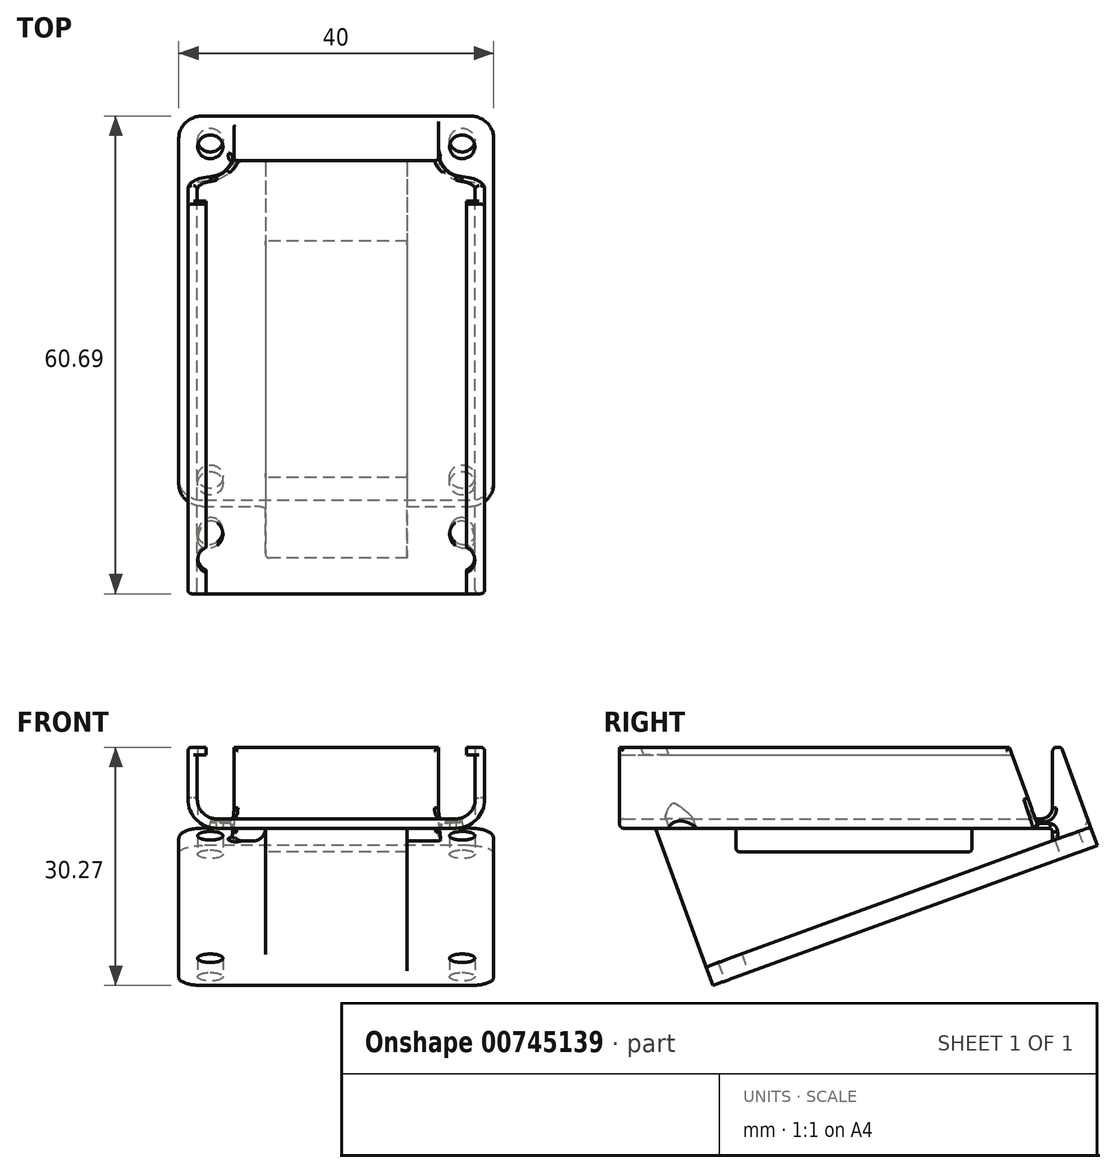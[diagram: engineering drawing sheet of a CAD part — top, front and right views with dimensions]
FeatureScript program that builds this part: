
annotation { "Feature Type Name" : "Feature", "Feature Type Description" : "" }
export const myFeature = defineFeature(function(context is Context, id is Id, definition is map)
    precondition{}
    {
        {
            var Q0;
            Q0=qCreatedBy(makeId("Front.planeOp"),FACE);
            var sketch = newSketch(context, id + "F0", { "sketchPlane" : qUnion([Q0])});
            skLineSegment(sketch, "E0", {"start": v(-15.15, 0) * mm, "end": v(15.15, 0) * mm});
            skLineSegment(sketch, "E1", {"start": v(-18.85, 3.7) * mm, "end": v(-18.85, 10.3) * mm});
            skLineSegment(sketch, "E2", {"start": v(-18.85, 10.3) * mm, "end": v(-16.55, 10.3) * mm});
            skLineSegment(sketch, "E3", {"start": v(-16.55, 10.3) * mm, "end": v(-16.55, 9.3) * mm});
            skLineSegment(sketch, "E4", {"start": v(-16.55, 9.3) * mm, "end": v(-17.65, 9.3) * mm});
            skLineSegment(sketch, "E5", {"start": v(-17.65, 9.3) * mm, "end": v(-17.65, 3.7) * mm});
            skLineSegment(sketch, "E6", {"start": v(17.65, 3.7) * mm, "end": v(17.65, 9.3) * mm});
            skLineSegment(sketch, "E7", {"start": v(17.65, 9.3) * mm, "end": v(16.55, 9.3) * mm});
            skLineSegment(sketch, "E8", {"start": v(16.55, 9.3) * mm, "end": v(16.55, 10.3) * mm});
            skLineSegment(sketch, "E9", {"start": v(16.55, 10.3) * mm, "end": v(18.85, 10.3) * mm});
            skLineSegment(sketch, "E10", {"start": v(18.85, 10.3) * mm, "end": v(18.85, 3.7) * mm});
            skLineSegment(sketch, "E11", {"start": v(-15.15, 1.2) * mm, "end": v(15.15, 1.2) * mm});
            skArc(sketch, "E12", {"start": v(17.65, 3.7) * mm, "mid": v(16.92, 1.93) * mm, "end": v(15.15, 1.2) * mm});
            skArc(sketch, "E13", {"start": v(-15.15, 1.2) * mm, "mid": v(-16.92, 1.93) * mm, "end": v(-17.65, 3.7) * mm});
            skArc(sketch, "E14", {"start": v(-18.85, 3.7) * mm, "mid": v(-17.77, 1.08) * mm, "end": v(-15.15, 0) * mm});
            skArc(sketch, "E15", {"start": v(15.15, 0) * mm, "mid": v(17.77, 1.08) * mm, "end": v(18.85, 3.7) * mm});
            skSolve(sketch);
        }
        {
            var Q0;
            Q0=qSketchRegion(id+"F0",true);
            extrude(context, id + "F1", {"entities" : qUnion([Q0]), "depth" : 55 * mm, "offsetDistance" : 25 * mm});
        }
        {
            var Q0;
            Q0=qCreatedBy(makeId("Right.planeOp"),FACE);
            var sketch = newSketch(context, id + "F2", { "sketchPlane" : qUnion([Q0])});
            skLineSegment(sketch, "E16", {"start": v(4.83, 0.16) * mm, "end": v(-44.03, -17.62) * mm});
            skPoint(sketch, "E17.0", {"position": v(-50.45, 0) * mm});
            skLineSegment(sketch, "E18", {"start": v(-50.45, 0) * mm, "end": v(-44.03, -17.62) * mm});
            skPoint(sketch, "E19.0", {"position": v(0, 10.3) * mm});
            skLineSegment(sketch, "E20", {"start": v(1.14, 10.3) * mm, "end": v(4.83, 0.16) * mm});
            skLineSegment(sketch, "E21", {"start": v(1.14, 10.3) * mm, "end": v(0, 10.3) * mm});
            skLineSegment(sketch, "E22", {"start": v(0, 0) * mm, "end": v(-50.45, 0) * mm});
            skLineSegment(sketch, "E23", {"start": v(4.83, 0.16) * mm, "end": v(5.69, -2.19) * mm});
            skLineSegment(sketch, "E24", {"start": v(5.69, -2.19) * mm, "end": v(-43.18, -19.97) * mm});
            skLineSegment(sketch, "E25", {"start": v(-43.18, -19.97) * mm, "end": v(-44.03, -17.62) * mm});
            skPoint(sketch, "E26", {"position": v(-25.22, 0) * mm});
            skLineSegment(sketch, "E27.bottom", {"start": v(-10.22, 0) * mm, "end": v(-40.22, 0) * mm});
            skLineSegment(sketch, "E27.top", {"start": v(-10.22, -3) * mm, "end": v(-40.22, -3) * mm});
            skLineSegment(sketch, "E27.left", {"start": v(-10.22, 0) * mm, "end": v(-10.22, -3) * mm});
            skLineSegment(sketch, "E27.right", {"start": v(-40.22, 0) * mm, "end": v(-40.22, -3) * mm});
            skLineSegment(sketch, "E28", {"start": v(0, 0) * mm, "end": v(0, 10.3) * mm});
            skLineSegment(sketch, "E29", {"start": v(0, 0) * mm, "end": v(0, -1.6) * mm});
            skSolve(sketch);
        }
        {
            var Q0;
            {var subQ0=sQuery(id+"F2.wireOp",EDGE,"E20");Q0=makeQuery(id+"F2.imprint","IMPRINT",FACE,{"disambiguationData":[TD([[makeQuery(id+"F2.imprint","IMPRINT",EDGE,{"derivedFrom":subQ0}),-1.0]])]});}
            var Q1;
            Q1=makeQuery(id+"F1.opExtrude","SWEPT_FACE",FACE,{"disambiguationData":[OSD([sQuery(id+"F0.wireOp",EDGE,"E1")])]});
            extrude(context, id + "F3", {"entities" : qUnion([Q0]), "operationType" : NewBodyOperationType.ADD, "endBound" : BoundingType.UP_TO_SURFACE, "oppositeDirection" : true, "depth" : 25 * mm, "endBoundEntityFace" : qUnion([Q1]), "offsetDistance" : 25 * mm});
        }
        {
            var Q0;
            {var subQ0=sQuery(id+"F2.wireOp",EDGE,"E20");Q0=makeQuery(id+"F2.imprint","IMPRINT",FACE,{"disambiguationData":[TD([[makeQuery(id+"F2.imprint","IMPRINT",EDGE,{"derivedFrom":subQ0}),-1.0]])]});}
            var Q1;
            Q1=makeQuery(id+"F1.opExtrude","SWEPT_FACE",FACE,{"disambiguationData":[OSD([sQuery(id+"F0.wireOp",EDGE,"E10")])]});
            extrude(context, id + "F4", {"entities" : qUnion([Q0]), "operationType" : NewBodyOperationType.ADD, "endBound" : BoundingType.UP_TO_SURFACE, "depth" : 25 * mm, "endBoundEntityFace" : qUnion([Q1]), "offsetDistance" : 25 * mm});
        }
        {
            var Q0;
            {var subQ0=sQuery(id+"F2.wireOp",EDGE,"E23");Q0=makeQuery(id+"F2.imprint","IMPRINT",FACE,{"disambiguationData":[TD([[makeQuery(id+"F2.imprint","IMPRINT",EDGE,{"derivedFrom":subQ0}),-1.0]])]});}
            extrude(context, id + "F5", {"entities" : qUnion([Q0]), "operationType" : NewBodyOperationType.ADD, "endBound" : BoundingType.SYMMETRIC, "depth" : 40 * mm, "offsetDistance" : 25 * mm});
        }
        {
            var Q0;
            {var subQ4=sQuery(id+"F2.wireOp",EDGE,"E18");Q0=makeQuery(id+"F2.imprint","IMPRINT",FACE,{"disambiguationData":[TD([[makeQuery(id+"F2.imprint","IMPRINT",EDGE,{"derivedFrom":subQ4}),1.0]])]});}
            extrude(context, id + "F6", {"entities" : qUnion([Q0]), "operationType" : NewBodyOperationType.ADD, "endBound" : BoundingType.SYMMETRIC, "depth" : 18 * mm, "offsetDistance" : 25 * mm});
        }
        {
            var Q0;
            Q0=makeQuery(id+"F5.opExtrude","SWEPT_FACE",FACE,{"disambiguationData":[OSD([sQuery(id+"F2.wireOp",EDGE,"E24")])]});
            var sketch = newSketch(context, id + "F7", { "sketchPlane" : qUnion([Q0])});
            skCircle(sketch, "E30", {"center": v(-16, -1.35) * mm, "radius": 1.6 * mm});
            skCircle(sketch, "E31", {"center": v(-16, 44.15) * mm, "radius": 1.6 * mm});
            skCircle(sketch, "E32", {"center": v(16, 44.15) * mm, "radius": 1.6 * mm});
            skCircle(sketch, "E33", {"center": v(16, -1.35) * mm, "radius": 1.6 * mm});
            skLineSegment(sketch, "E34", {"start": v(-16, 44.15) * mm, "end": v(-16, 47.4) * mm, "construction": true});
            skLineSegment(sketch, "E35", {"start": v(-16, -1.35) * mm, "end": v(-16, -4.6) * mm, "construction": true});
            skSolve(sketch);
        }
        {
            var Q0;
            Q0 = qSketchRegion(id + "F7", true);
            extrude(context, id + "F8", {"entities" : qUnion([Q0]), "operationType" : NewBodyOperationType.REMOVE, "endBound" : BoundingType.THROUGH_ALL, "oppositeDirection" : true, "depth" : 25 * mm, "offsetDistance" : 25 * mm});
        }
        {
            var Q0;
            {var subQ2=sQuery(id+"F2.wireOp",EDGE,"E16");var subQ4=sQuery(id+"F0.wireOp",EDGE,"E10");Q0=makeQuery(id+"F6.boolean.opBoolean","SPLIT",FACE,{"disambiguationData":[TD([makeQuery(id+"F1.opExtrude","SWEPT_FACE",FACE,{"disambiguationData":[OSD([subQ4])]})])],"derivedFrom":makeQuery(id+"F5.opExtrude","SWEPT_FACE",FACE,{"disambiguationData":[OSD([subQ2])]})});}
            cPlane(context, id + "F9", {"entities" : qUnion([Q0]), "cplaneType" : CPlaneType.OFFSET, "offset" : 0 * mm, "width" : 150 * mm, "height" : 150 * mm});
        }
        {
            var Q0;
            Q0=qCreatedBy(id+"F9.planeOp",FACE);
            var sketch = newSketch(context, id + "F10", { "sketchPlane" : qUnion([Q0])});
            skCircle(sketch, "E36.0", {"center": v(16, 1.35) * mm, "radius": 1.6 * mm});
            skCircle(sketch, "E37.0", {"center": v(-16, 1.35) * mm, "radius": 1.6 * mm});
            skLineSegment(sketch, "E38.0", {"start": v(20, 4.6) * mm, "end": v(-20, 4.6) * mm});
            skLineSegment(sketch, "E39.0", {"start": v(20, 4.6) * mm, "end": v(20, -47.4) * mm});
            skLineSegment(sketch, "E40.0", {"start": v(-20, 4.6) * mm, "end": v(-20, -47.4) * mm});
            skArc(sketch, "E41", {"start": v(-16, -1.65) * mm, "mid": v(-13.88, -0.78) * mm, "end": v(-13, 1.35) * mm});
            skArc(sketch, "E42", {"start": v(13, 1.35) * mm, "mid": v(13.88, -0.78) * mm, "end": v(16, -1.65) * mm});
            skLineSegment(sketch, "E43", {"start": v(16, -1.65) * mm, "end": v(20, -1.65) * mm});
            skLineSegment(sketch, "E44", {"start": v(13, 1.35) * mm, "end": v(13, 4.6) * mm});
            skLineSegment(sketch, "E45", {"start": v(-16, -1.65) * mm, "end": v(-20, -1.65) * mm});
            skLineSegment(sketch, "E46", {"start": v(-13, 1.35) * mm, "end": v(-13, 4.6) * mm});
            skSolve(sketch);
        }
        {
            var Q0;
            Q0 = qSketchRegion(id + "F10", true);
            extrude(context, id + "F11", {"entities" : qUnion([Q0]), "operationType" : NewBodyOperationType.REMOVE, "endBound" : BoundingType.THROUGH_ALL, "depth" : 25 * mm, "offsetDistance" : 25 * mm});
        }
        {
            var Q0;
            Q0=makeQuery(id+"F5.opExtrude","CAP_EDGE",EDGE,{"disambiguationData":[OSD([sQuery(id+"F2.wireOp",EDGE,"E25")])],"isStart":true});
            var Q1;
            Q1=makeQuery(id+"F5.opExtrude","CAP_EDGE",EDGE,{"disambiguationData":[OSD([sQuery(id+"F2.wireOp",EDGE,"E23")])],"isStart":true});
            var Q2;
            Q2=makeQuery(id+"F5.opExtrude","CAP_EDGE",EDGE,{"disambiguationData":[OSD([sQuery(id+"F2.wireOp",EDGE,"E23")])],"isStart":false});
            var Q3;
            Q3=makeQuery(id+"F5.opExtrude","CAP_EDGE",EDGE,{"disambiguationData":[OSD([sQuery(id+"F2.wireOp",EDGE,"E25")])],"isStart":false});
            fillet(context, id + "F12", {"entities" : qUnion([Q0, Q1, Q2, Q3]), "radius" : 3 * mm, "tangentPropagation" : true, "allowEdgeOverflow" : false});
        }
        {
            var Q0;
            Q0=makeQuery(id+"F6.opExtrude","CAP_EDGE",EDGE,{"disambiguationData":[OSD([sQuery(id+"F2.wireOp",EDGE,"E16")])],"isStart":false});
            var Q1;
            {var subQ0=sQuery(id+"F2.wireOp",EDGE,"E22");Q1=makeQuery(id+"F6.opExtrude","CAP_EDGE",EDGE,{"disambiguationData":[OSD([subQ0]),TDD([makeQuery(id+"F2.imprint","IMPRINT",EDGE,{"disambiguationData":[TD([[makeQuery(id+"F2.imprint","INTERSECT",VERTEX,{"derivedFrom":[subQ0,sQuery(id+"F2.wireOp",EDGE,"E28"),sQuery(id+"F2.wireOp",EDGE,"E29")]}),-1.0]])],"derivedFrom":subQ0})])],"isStart":false});}
            var Q2;
            {var subQ0=sQuery(id+"F2.wireOp",EDGE,"E22");Q2=makeQuery(id+"F6.opExtrude","CAP_EDGE",EDGE,{"disambiguationData":[OSD([subQ0]),TDD([makeQuery(id+"F2.imprint","IMPRINT",EDGE,{"disambiguationData":[TD([[makeQuery(id+"F2.imprint","INTERSECT",VERTEX,{"derivedFrom":[sQuery(id+"F2.wireOp",EDGE,"E18"),subQ0]}),1.0]])],"derivedFrom":subQ0})])],"isStart":false});}
            var Q3;
            {var subQ0=sQuery(id+"F2.wireOp",EDGE,"E22");Q3=makeQuery(id+"F6.opExtrude","CAP_EDGE",EDGE,{"disambiguationData":[OSD([subQ0]),TDD([makeQuery(id+"F2.imprint","IMPRINT",EDGE,{"disambiguationData":[TD([[makeQuery(id+"F2.imprint","INTERSECT",VERTEX,{"derivedFrom":[sQuery(id+"F2.wireOp",EDGE,"E18"),subQ0]}),1.0]])],"derivedFrom":subQ0})])],"isStart":true});}
            var Q4;
            Q4=makeQuery(id+"F6.opExtrude","CAP_EDGE",EDGE,{"disambiguationData":[OSD([sQuery(id+"F2.wireOp",EDGE,"E16")])],"isStart":true});
            var Q5;
            {var subQ0=sQuery(id+"F2.wireOp",EDGE,"E22");Q5=makeQuery(id+"F6.opExtrude","CAP_EDGE",EDGE,{"disambiguationData":[OSD([subQ0]),TDD([makeQuery(id+"F2.imprint","IMPRINT",EDGE,{"disambiguationData":[TD([[makeQuery(id+"F2.imprint","INTERSECT",VERTEX,{"derivedFrom":[subQ0,sQuery(id+"F2.wireOp",EDGE,"E28"),sQuery(id+"F2.wireOp",EDGE,"E29")]}),-1.0]])],"derivedFrom":subQ0})])],"isStart":true});}
            var Q6;
            {var subQ0=sQuery(id+"F0.wireOp",EDGE,"E11");var subQ2=makeQuery(id+"F1.opExtrude","CAP_EDGE",EDGE,{"disambiguationData":[OSD([subQ0])],"isStart":true});Q6=makeQuery(id+"F4.boolean.opBoolean","MERGE",EDGE,{"derivedFrom":[makeQuery(id+"F3.boolean.opBoolean","SPLIT",EDGE,{"disambiguationData":[topologyDisambiguationEdgeConnected([makeQuery(id+"F1.opExtrude","CAP_FACE",FACE,{"disambiguationData":[OSD([sQuery(id+"F0.wireOp",EDGE,"E0"),sQuery(id+"F0.wireOp",EDGE,"E1"),sQuery(id+"F0.wireOp",EDGE,"E2"),sQuery(id+"F0.wireOp",EDGE,"E3"),sQuery(id+"F0.wireOp",EDGE,"E4"),sQuery(id+"F0.wireOp",EDGE,"E5"),sQuery(id+"F0.wireOp",EDGE,"E6"),sQuery(id+"F0.wireOp",EDGE,"E7"),sQuery(id+"F0.wireOp",EDGE,"E8"),sQuery(id+"F0.wireOp",EDGE,"E9"),sQuery(id+"F0.wireOp",EDGE,"E10"),subQ0,sQuery(id+"F0.wireOp",EDGE,"E12"),sQuery(id+"F0.wireOp",EDGE,"E13"),sQuery(id+"F0.wireOp",EDGE,"E14"),sQuery(id+"F0.wireOp",EDGE,"E15")])],"isStart":true})])],"derivedFrom":subQ2}),makeQuery(id+"F3.boolean.opBoolean","SPLIT",EDGE,{"disambiguationData":[topologyDisambiguationEdgeConnected([makeQuery(id+"F3.opExtrude","SWEPT_FACE",FACE,{"disambiguationData":[OSD([sQuery(id+"F2.wireOp",EDGE,"E28"),sQuery(id+"F2.wireOp",EDGE,"E29")])]})])],"derivedFrom":subQ2})]});}
            fillet(context, id + "F13", {"entities" : qUnion([Q0, Q1, Q2, Q3, Q4, Q5, Q6]), "radius" : 1.5 * mm, "tangentPropagation" : true, "allowEdgeOverflow" : false});
        }
        {
            var Q0;
            Q0=makeQuery(id+"F5.opExtrude","CAP_EDGE",EDGE,{"disambiguationData":[OSD([sQuery(id+"F2.wireOp",EDGE,"E16")])],"isStart":true});
            var Q1;
            Q1=makeQuery(id+"F5.opExtrude","CAP_EDGE",EDGE,{"disambiguationData":[OSD([sQuery(id+"F2.wireOp",EDGE,"E16")])],"isStart":false});
            var Q2;
            Q2=makeQuery(id+"F6.opExtrude","SWEPT_EDGE",EDGE,{"disambiguationData":[OSD([sQuery(id+"F2.wireOp",EDGE,"E18"),sQuery(id+"F2.wireOp",EDGE,"E22")])]});
            var Q3;
            Q3=makeQuery(id+"F6.opExtrude","SWEPT_EDGE",EDGE,{"disambiguationData":[OSD([sQuery(id+"F2.wireOp",EDGE,"E22"),sQuery(id+"F2.wireOp",EDGE,"E27.bottom"),sQuery(id+"F2.wireOp",EDGE,"E27.right")])]});
            var Q4;
            Q4=makeQuery(id+"F6.opExtrude","SWEPT_EDGE",EDGE,{"disambiguationData":[OSD([sQuery(id+"F2.wireOp",EDGE,"E27.top"),sQuery(id+"F2.wireOp",EDGE,"E27.right")])]});
            var Q5;
            Q5=makeQuery(id+"F6.opExtrude","SWEPT_EDGE",EDGE,{"disambiguationData":[OSD([sQuery(id+"F2.wireOp",EDGE,"E27.top"),sQuery(id+"F2.wireOp",EDGE,"E27.left")])]});
            var Q6;
            Q6=makeQuery(id+"F6.opExtrude","SWEPT_EDGE",EDGE,{"disambiguationData":[OSD([sQuery(id+"F2.wireOp",EDGE,"E22"),sQuery(id+"F2.wireOp",EDGE,"E27.bottom"),sQuery(id+"F2.wireOp",EDGE,"E27.left")])]});
            var Q7;
            Q7=makeQuery(id+"F11.boolean.opBoolean","COPY",EDGE,{"derivedFrom":makeQuery(id+"F11.opExtrude","SWEPT_EDGE",EDGE,{"disambiguationData":[OSD([sQuery(id+"F10.wireOp",EDGE,"E38.0"),sQuery(id+"F10.wireOp",EDGE,"E46")])]})});
            var Q8;
            {var subQ0=sQuery(id+"F2.wireOp",EDGE,"E21");var subQ1=sQuery(id+"F2.wireOp",EDGE,"E20");Q8=makeQuery(id+"F4.boolean.opBoolean","MERGE",EDGE,{"derivedFrom":[makeQuery(id+"F3.opExtrude","SWEPT_EDGE",EDGE,{"disambiguationData":[OSD([subQ1,subQ0])]}),makeQuery(id+"F4.opExtrude","SWEPT_EDGE",EDGE,{"disambiguationData":[OSD([subQ1,subQ0])]})]});}
            var Q9;
            Q9=makeQuery(id+"F11.boolean.opBoolean","COPY",EDGE,{"derivedFrom":makeQuery(id+"F11.opExtrude","SWEPT_EDGE",EDGE,{"disambiguationData":[OSD([sQuery(id+"F10.wireOp",EDGE,"E38.0"),sQuery(id+"F10.wireOp",EDGE,"E44")])]})});
            var Q10;
            {var subQ0=sQuery(id+"F2.wireOp",EDGE,"E28");var subQ1=sQuery(id+"F2.wireOp",EDGE,"E21");Q10=makeQuery(id+"F4.boolean.opBoolean","MERGE",EDGE,{"derivedFrom":[makeQuery(id+"F3.opExtrude","SWEPT_EDGE",EDGE,{"disambiguationData":[OSD([subQ1,subQ0])]}),makeQuery(id+"F4.opExtrude","SWEPT_EDGE",EDGE,{"disambiguationData":[OSD([subQ1,subQ0])]})]});}
            var Q11;
            {var subQ0=sQuery(id+"F2.wireOp",EDGE,"E29");var subQ1=sQuery(id+"F2.wireOp",EDGE,"E28");var subQ4=sQuery(id+"F0.wireOp",EDGE,"E2");Q11=makeQuery(id+"F11.boolean.opBoolean","INTERSECT",EDGE,{"derivedFrom":[makeQuery(id+"F4.boolean.opBoolean","MERGE",FACE,{"derivedFrom":[makeQuery(id+"F3.boolean.opBoolean","SPLIT",FACE,{"disambiguationData":[TD([makeQuery(id+"F1.opExtrude","SWEPT_FACE",FACE,{"disambiguationData":[OSD([subQ4])]})])],"derivedFrom":makeQuery(id+"F3.opExtrude","SWEPT_FACE",FACE,{"disambiguationData":[OSD([subQ1,subQ0])]})}),makeQuery(id+"F4.opExtrude","SWEPT_FACE",FACE,{"disambiguationData":[OSD([subQ1,subQ0])]})]}),makeQuery(id+"F11.opExtrude","SWEPT_FACE",FACE,{"disambiguationData":[OSD([sQuery(id+"F10.wireOp",EDGE,"E44")])]})]});}
            var Q12;
            {var subQ0=sQuery(id+"F2.wireOp",EDGE,"E29");var subQ1=sQuery(id+"F2.wireOp",EDGE,"E28");var subQ4=sQuery(id+"F0.wireOp",EDGE,"E2");Q12=makeQuery(id+"F11.boolean.opBoolean","INTERSECT",EDGE,{"derivedFrom":[makeQuery(id+"F4.boolean.opBoolean","MERGE",FACE,{"derivedFrom":[makeQuery(id+"F3.boolean.opBoolean","SPLIT",FACE,{"disambiguationData":[TD([makeQuery(id+"F1.opExtrude","SWEPT_FACE",FACE,{"disambiguationData":[OSD([subQ4])]})])],"derivedFrom":makeQuery(id+"F3.opExtrude","SWEPT_FACE",FACE,{"disambiguationData":[OSD([subQ1,subQ0])]})}),makeQuery(id+"F4.opExtrude","SWEPT_FACE",FACE,{"disambiguationData":[OSD([subQ1,subQ0])]})]}),makeQuery(id+"F11.opExtrude","SWEPT_FACE",FACE,{"disambiguationData":[OSD([sQuery(id+"F10.wireOp",EDGE,"E46")])]})]});}
            var Q13;
            {var subQ0=sQuery(id+"F0.wireOp",EDGE,"E1");Q13=makeQuery(id+"F3.boolean.opBoolean","MERGE",EDGE,{"derivedFrom":[makeQuery(id+"F1.opExtrude","SWEPT_EDGE",EDGE,{"disambiguationData":[OSD([subQ0,sQuery(id+"F0.wireOp",EDGE,"E2")])]}),makeQuery(id+"F3.opExtrude","TWEAK_EDGE",EDGE,{"derivedFrom":[makeQuery(id+"F1.opExtrude","SWEPT_FACE",FACE,{"disambiguationData":[OSD([subQ0])]}),makeQuery(id+"F2.imprint","IMPRINT",EDGE,{"derivedFrom":sQuery(id+"F2.wireOp",EDGE,"E21")})]})]});}
            var Q14;
            {var subQ0=sQuery(id+"F0.wireOp",EDGE,"E10");Q14=makeQuery(id+"F4.boolean.opBoolean","MERGE",EDGE,{"derivedFrom":[makeQuery(id+"F1.opExtrude","SWEPT_EDGE",EDGE,{"disambiguationData":[OSD([sQuery(id+"F0.wireOp",EDGE,"E9"),subQ0])]}),makeQuery(id+"F4.opExtrude","TWEAK_EDGE",EDGE,{"derivedFrom":[makeQuery(id+"F1.opExtrude","SWEPT_FACE",FACE,{"disambiguationData":[OSD([subQ0])]}),makeQuery(id+"F2.imprint","IMPRINT",EDGE,{"derivedFrom":sQuery(id+"F2.wireOp",EDGE,"E21")})]})]});}
            var Q15;
            {var subQ0=sQuery(id+"F0.wireOp",EDGE,"E10");Q15=makeQuery(id+"F11.boolean.opBoolean","INTERSECT",EDGE,{"derivedFrom":[makeQuery(id+"F4.boolean.opBoolean","MERGE",FACE,{"derivedFrom":[makeQuery(id+"F1.opExtrude","SWEPT_FACE",FACE,{"disambiguationData":[OSD([subQ0])]}),makeQuery(id+"F4.opExtrude","CAP_FACE",FACE,{"disambiguationData":[OSD([subQ0])],"isStart":false})]}),makeQuery(id+"F11.opExtrude","SWEPT_FACE",FACE,{"disambiguationData":[OSD([sQuery(id+"F10.wireOp",EDGE,"E43")])]})]});}
            var Q16;
            {var subQ0=sQuery(id+"F0.wireOp",EDGE,"E1");Q16=makeQuery(id+"F11.boolean.opBoolean","INTERSECT",EDGE,{"derivedFrom":[makeQuery(id+"F3.boolean.opBoolean","MERGE",FACE,{"derivedFrom":[makeQuery(id+"F1.opExtrude","SWEPT_FACE",FACE,{"disambiguationData":[OSD([subQ0])]}),makeQuery(id+"F3.opExtrude","CAP_FACE",FACE,{"disambiguationData":[OSD([subQ0])],"isStart":false})]}),makeQuery(id+"F11.opExtrude","SWEPT_FACE",FACE,{"disambiguationData":[OSD([sQuery(id+"F10.wireOp",EDGE,"E45")])]})]});}
            var Q17;
            {var subQ0=sQuery(id+"F0.wireOp",EDGE,"E0");var subQ1=makeQuery(id+"F1.opExtrude","SWEPT_FACE",FACE,{"disambiguationData":[OSD([subQ0])]});var subQ2=sQuery(id+"F2.wireOp",EDGE,"E29");var subQ8=sQuery(id+"F0.wireOp",EDGE,"E1");var subQ10=makeQuery(id+"F1.opExtrude","SWEPT_FACE",FACE,{"disambiguationData":[OSD([subQ8])]});var subQ11=sQuery(id+"F2.wireOp",EDGE,"E28");Q17=makeQuery(id+"F11.boolean.opBoolean","INTERSECT",EDGE,{"derivedFrom":[makeQuery(id+"F8.boolean.opBoolean","SPLIT",FACE,{"disambiguationData":[TD([subQ1])],"derivedFrom":makeQuery(id+"F6.boolean.opBoolean","SPLIT",FACE,{"disambiguationData":[TD([subQ10])],"derivedFrom":makeQuery(id+"F4.boolean.opBoolean","MERGE",FACE,{"derivedFrom":[makeQuery(id+"F3.boolean.opBoolean","SPLIT",FACE,{"disambiguationData":[TD([subQ1])],"derivedFrom":makeQuery(id+"F3.opExtrude","SWEPT_FACE",FACE,{"disambiguationData":[OSD([subQ11,subQ2])]})}),makeQuery(id+"F4.opExtrude","SWEPT_FACE",FACE,{"disambiguationData":[OSD([subQ11,subQ2])]})]})})}),makeQuery(id+"F11.opExtrude","SWEPT_FACE",FACE,{"disambiguationData":[OSD([sQuery(id+"F10.wireOp",EDGE,"E41")])]})]});}
            var Q18;
            {var subQ0=sQuery(id+"F0.wireOp",EDGE,"E0");var subQ1=makeQuery(id+"F1.opExtrude","SWEPT_FACE",FACE,{"disambiguationData":[OSD([subQ0])]});var subQ4=sQuery(id+"F2.wireOp",EDGE,"E29");var subQ7=sQuery(id+"F0.wireOp",EDGE,"E10");var subQ8=sQuery(id+"F2.wireOp",EDGE,"E28");Q18=makeQuery(id+"F11.boolean.opBoolean","INTERSECT",EDGE,{"derivedFrom":[makeQuery(id+"F8.boolean.opBoolean","SPLIT",FACE,{"disambiguationData":[TD([subQ1])],"derivedFrom":makeQuery(id+"F6.boolean.opBoolean","SPLIT",FACE,{"disambiguationData":[TD([makeQuery(id+"F1.opExtrude","SWEPT_FACE",FACE,{"disambiguationData":[OSD([subQ7])]})])],"derivedFrom":makeQuery(id+"F4.boolean.opBoolean","MERGE",FACE,{"derivedFrom":[makeQuery(id+"F3.boolean.opBoolean","SPLIT",FACE,{"disambiguationData":[TD([subQ1])],"derivedFrom":makeQuery(id+"F3.opExtrude","SWEPT_FACE",FACE,{"disambiguationData":[OSD([subQ8,subQ4])]})}),makeQuery(id+"F4.opExtrude","SWEPT_FACE",FACE,{"disambiguationData":[OSD([subQ8,subQ4])]})]})})}),makeQuery(id+"F11.opExtrude","SWEPT_FACE",FACE,{"disambiguationData":[OSD([sQuery(id+"F10.wireOp",EDGE,"E42")])]})]});}
            var Q19;
            {var subQ0=sQuery(id+"F2.wireOp",EDGE,"E29");var subQ1=sQuery(id+"F2.wireOp",EDGE,"E28");var subQ2=makeQuery(id+"F3.opExtrude","SWEPT_FACE",FACE,{"disambiguationData":[OSD([subQ1,subQ0])]});var subQ3=sQuery(id+"F0.wireOp",EDGE,"E15");var subQ4=sQuery(id+"F0.wireOp",EDGE,"E0");var subQ6=makeQuery(id+"F1.opExtrude","CAP_EDGE",EDGE,{"disambiguationData":[OSD([subQ4])],"isStart":true});Q19=makeQuery(id+"F6.boolean.opBoolean","SPLIT",EDGE,{"disambiguationData":[TD([makeQuery(id+"F1.opExtrude","SWEPT_FACE",FACE,{"disambiguationData":[OSD([subQ3])]})])],"derivedFrom":makeQuery(id+"F4.boolean.opBoolean","MERGE",EDGE,{"derivedFrom":[makeQuery(id+"F3.boolean.opBoolean","SPLIT",EDGE,{"disambiguationData":[topologyDisambiguationEdgeConnected([makeQuery(id+"F1.opExtrude","CAP_FACE",FACE,{"disambiguationData":[OSD([subQ4,sQuery(id+"F0.wireOp",EDGE,"E1"),sQuery(id+"F0.wireOp",EDGE,"E2"),sQuery(id+"F0.wireOp",EDGE,"E3"),sQuery(id+"F0.wireOp",EDGE,"E4"),sQuery(id+"F0.wireOp",EDGE,"E5"),sQuery(id+"F0.wireOp",EDGE,"E6"),sQuery(id+"F0.wireOp",EDGE,"E7"),sQuery(id+"F0.wireOp",EDGE,"E8"),sQuery(id+"F0.wireOp",EDGE,"E9"),sQuery(id+"F0.wireOp",EDGE,"E10"),sQuery(id+"F0.wireOp",EDGE,"E11"),sQuery(id+"F0.wireOp",EDGE,"E12"),sQuery(id+"F0.wireOp",EDGE,"E13"),sQuery(id+"F0.wireOp",EDGE,"E14"),subQ3])],"isStart":true})])],"derivedFrom":subQ6}),makeQuery(id+"F3.boolean.opBoolean","SPLIT",EDGE,{"disambiguationData":[topologyDisambiguationEdgeConnected([subQ2])],"derivedFrom":subQ6})]})});}
            var Q20;
            {var subQ0=sQuery(id+"F2.wireOp",EDGE,"E29");var subQ1=sQuery(id+"F2.wireOp",EDGE,"E16");var subQ2=makeQuery(id+"F6.opExtrude","CAP_FACE",FACE,{"disambiguationData":[OSD([subQ1,sQuery(id+"F2.wireOp",EDGE,"E18"),sQuery(id+"F2.wireOp",EDGE,"E22"),sQuery(id+"F2.wireOp",EDGE,"E27.top"),sQuery(id+"F2.wireOp",EDGE,"E27.left"),sQuery(id+"F2.wireOp",EDGE,"E27.right"),subQ0])],"isStart":false});var subQ7=sQuery(id+"F0.wireOp",EDGE,"E10");Q20=makeQuery(id+"F8.boolean.opBoolean","SPLIT",EDGE,{"disambiguationData":[TD([subQ2])],"derivedFrom":makeQuery(id+"F6.boolean.opBoolean","SPLIT",EDGE,{"disambiguationData":[TD([makeQuery(id+"F1.opExtrude","SWEPT_FACE",FACE,{"disambiguationData":[OSD([subQ7])]})])],"derivedFrom":makeQuery(id+"F4.boolean.opBoolean","MERGE",EDGE,{"derivedFrom":[makeQuery(id+"F3.opExtrude","SWEPT_EDGE",EDGE,{"disambiguationData":[OSD([subQ1,subQ0])]}),makeQuery(id+"F4.opExtrude","SWEPT_EDGE",EDGE,{"disambiguationData":[OSD([subQ1,subQ0])]})]})})});}
            var Q21;
            Q21=makeQuery(id+"F11.boolean.opBoolean","COPY",EDGE,{"derivedFrom":makeQuery(id+"F11.opExtrude","CAP_EDGE",EDGE,{"disambiguationData":[OSD([sQuery(id+"F10.wireOp",EDGE,"E46")])],"isStart":true})});
            var Q22;
            {var subQ0=sQuery(id+"F2.wireOp",EDGE,"E29");var subQ1=sQuery(id+"F2.wireOp",EDGE,"E28");var subQ2=makeQuery(id+"F3.opExtrude","SWEPT_FACE",FACE,{"disambiguationData":[OSD([subQ1,subQ0])]});var subQ3=sQuery(id+"F0.wireOp",EDGE,"E14");var subQ4=sQuery(id+"F0.wireOp",EDGE,"E0");var subQ6=makeQuery(id+"F1.opExtrude","CAP_EDGE",EDGE,{"disambiguationData":[OSD([subQ4])],"isStart":true});Q22=makeQuery(id+"F6.boolean.opBoolean","SPLIT",EDGE,{"disambiguationData":[TD([makeQuery(id+"F1.opExtrude","SWEPT_FACE",FACE,{"disambiguationData":[OSD([subQ3])]})])],"derivedFrom":makeQuery(id+"F4.boolean.opBoolean","MERGE",EDGE,{"derivedFrom":[makeQuery(id+"F3.boolean.opBoolean","SPLIT",EDGE,{"disambiguationData":[topologyDisambiguationEdgeConnected([makeQuery(id+"F1.opExtrude","CAP_FACE",FACE,{"disambiguationData":[OSD([subQ4,sQuery(id+"F0.wireOp",EDGE,"E1"),sQuery(id+"F0.wireOp",EDGE,"E2"),sQuery(id+"F0.wireOp",EDGE,"E3"),sQuery(id+"F0.wireOp",EDGE,"E4"),sQuery(id+"F0.wireOp",EDGE,"E5"),sQuery(id+"F0.wireOp",EDGE,"E6"),sQuery(id+"F0.wireOp",EDGE,"E7"),sQuery(id+"F0.wireOp",EDGE,"E8"),sQuery(id+"F0.wireOp",EDGE,"E9"),sQuery(id+"F0.wireOp",EDGE,"E10"),sQuery(id+"F0.wireOp",EDGE,"E11"),sQuery(id+"F0.wireOp",EDGE,"E12"),sQuery(id+"F0.wireOp",EDGE,"E13"),subQ3,sQuery(id+"F0.wireOp",EDGE,"E15")])],"isStart":true})])],"derivedFrom":subQ6}),makeQuery(id+"F3.boolean.opBoolean","SPLIT",EDGE,{"disambiguationData":[topologyDisambiguationEdgeConnected([subQ2])],"derivedFrom":subQ6})]})});}
            var Q23;
            Q23=makeQuery(id+"F1.opExtrude","CAP_EDGE",EDGE,{"disambiguationData":[OSD([sQuery(id+"F0.wireOp",EDGE,"E11")])],"isStart":false});
            var Q24;
            Q24=makeQuery(id+"F1.opExtrude","CAP_EDGE",EDGE,{"disambiguationData":[OSD([sQuery(id+"F0.wireOp",EDGE,"E0")])],"isStart":false});
            fillet(context, id + "F14", {"entities" : qUnion([Q0, Q1, Q2, Q3, Q4, Q5, Q6, Q7, Q8, Q9, Q10, Q11, Q12, Q13, Q14, Q15, Q16, Q17, Q18, Q19, Q20, Q21, Q22, Q23, Q24]), "radius" : 0.5 * mm, "tangentPropagation" : true, "allowEdgeOverflow" : false});
        }
    });
